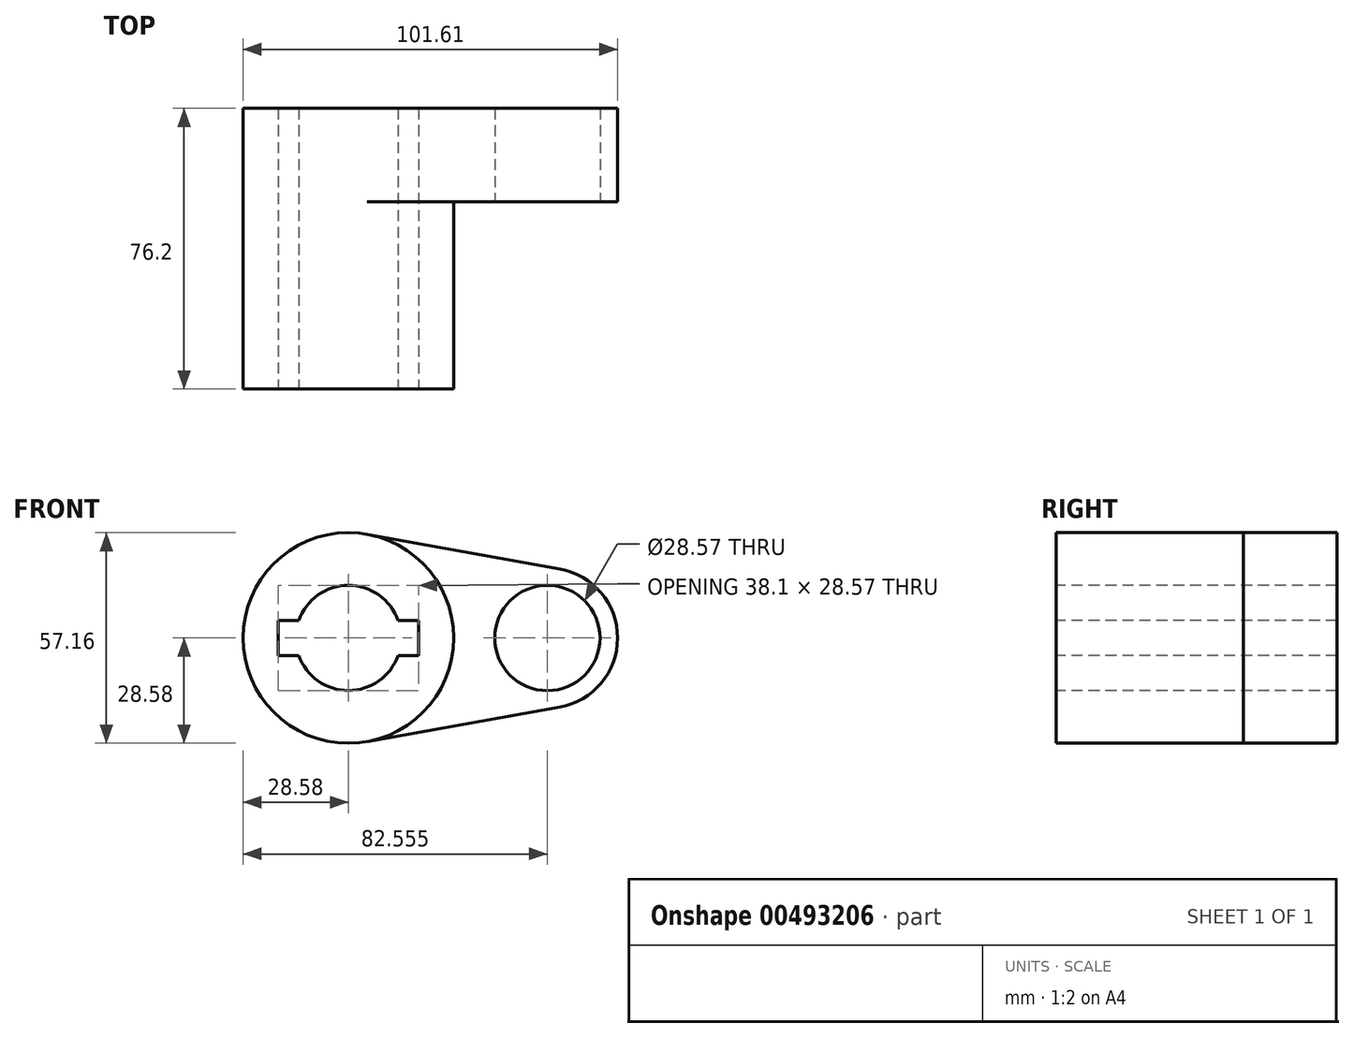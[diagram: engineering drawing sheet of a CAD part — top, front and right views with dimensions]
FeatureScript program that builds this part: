
annotation { "Feature Type Name" : "Feature", "Feature Type Description" : "" }
export const myFeature = defineFeature(function(context is Context, id is Id, definition is map)
    precondition{}
    {
        {
            var Q0;
            Q0=qCreatedBy(makeId("Front.planeOp"),FACE);
            var sketch = newSketch(context, id + "F0", { "sketchPlane" : qUnion([Q0])});
            skCircle(sketch, "E0", {"center": v(0, 0) * mm, "radius": 28.58 * mm});
            skCircle(sketch, "E1", {"center": v(53.98, 0) * mm, "radius": 19.05 * mm});
            skLineSegment(sketch, "E2", {"start": v(5.04, 28.13) * mm, "end": v(57.34, 18.75) * mm});
            skLineSegment(sketch, "E3", {"start": v(5.04, -28.13) * mm, "end": v(57.34, -18.75) * mm});
            skCircle(sketch, "E4", {"center": v(0, 0) * mm, "radius": 14.29 * mm});
            skCircle(sketch, "E5", {"center": v(53.98, 0) * mm, "radius": 14.29 * mm});
            skLineSegment(sketch, "E6.bottom", {"start": v(-19.05, 4.76) * mm, "end": v(19.05, 4.76) * mm});
            skLineSegment(sketch, "E6.top", {"start": v(-19.05, -4.76) * mm, "end": v(19.05, -4.76) * mm});
            skLineSegment(sketch, "E6.left", {"start": v(-19.05, 4.76) * mm, "end": v(-19.05, -4.76) * mm});
            skLineSegment(sketch, "E6.right", {"start": v(19.05, 4.76) * mm, "end": v(19.05, -4.76) * mm});
            skSolve(sketch);
        }
        {
            var Q0;
            {var subQ7=sQuery(id+"F0.wireOp",EDGE,"E6.left");Q0=makeQuery(id+"F0.imprint","IMPRINT",FACE,{"disambiguationData":[TD([[makeQuery(id+"F0.imprint","IMPRINT",EDGE,{"derivedFrom":subQ7}),-1.0]])]});}
            var Q1;
            {var subQ0=sQuery(id+"F0.wireOp",EDGE,"E2");Q1=makeQuery(id+"F0.imprint","IMPRINT",FACE,{"disambiguationData":[TD([[makeQuery(id+"F0.imprint","IMPRINT",EDGE,{"derivedFrom":subQ0}),-1.0]])]});}
            var Q2;
            Q2=makeQuery(id+"F0.imprint","IMPRINT",FACE,{"disambiguationData":[TD([[makeQuery(id+"F0.imprint","IMPRINT",EDGE,{"derivedFrom":sQuery(id+"F0.wireOp",EDGE,"E5")}),-1.0]])]});
            extrude(context, id + "F1", {"entities" : qUnion([Q0, Q1, Q2]), "oppositeDirection" : true, "depth" : 25.4 * mm});
        }
        {
            var Q0;
            {var subQ7=sQuery(id+"F0.wireOp",EDGE,"E6.left");Q0=makeQuery(id+"F0.imprint","IMPRINT",FACE,{"disambiguationData":[TD([[makeQuery(id+"F0.imprint","IMPRINT",EDGE,{"derivedFrom":subQ7}),-1.0]])]});}
            extrude(context, id + "F2", {"entities" : qUnion([Q0]), "operationType" : NewBodyOperationType.ADD, "depth" : 50.8 * mm});
        }
    });
